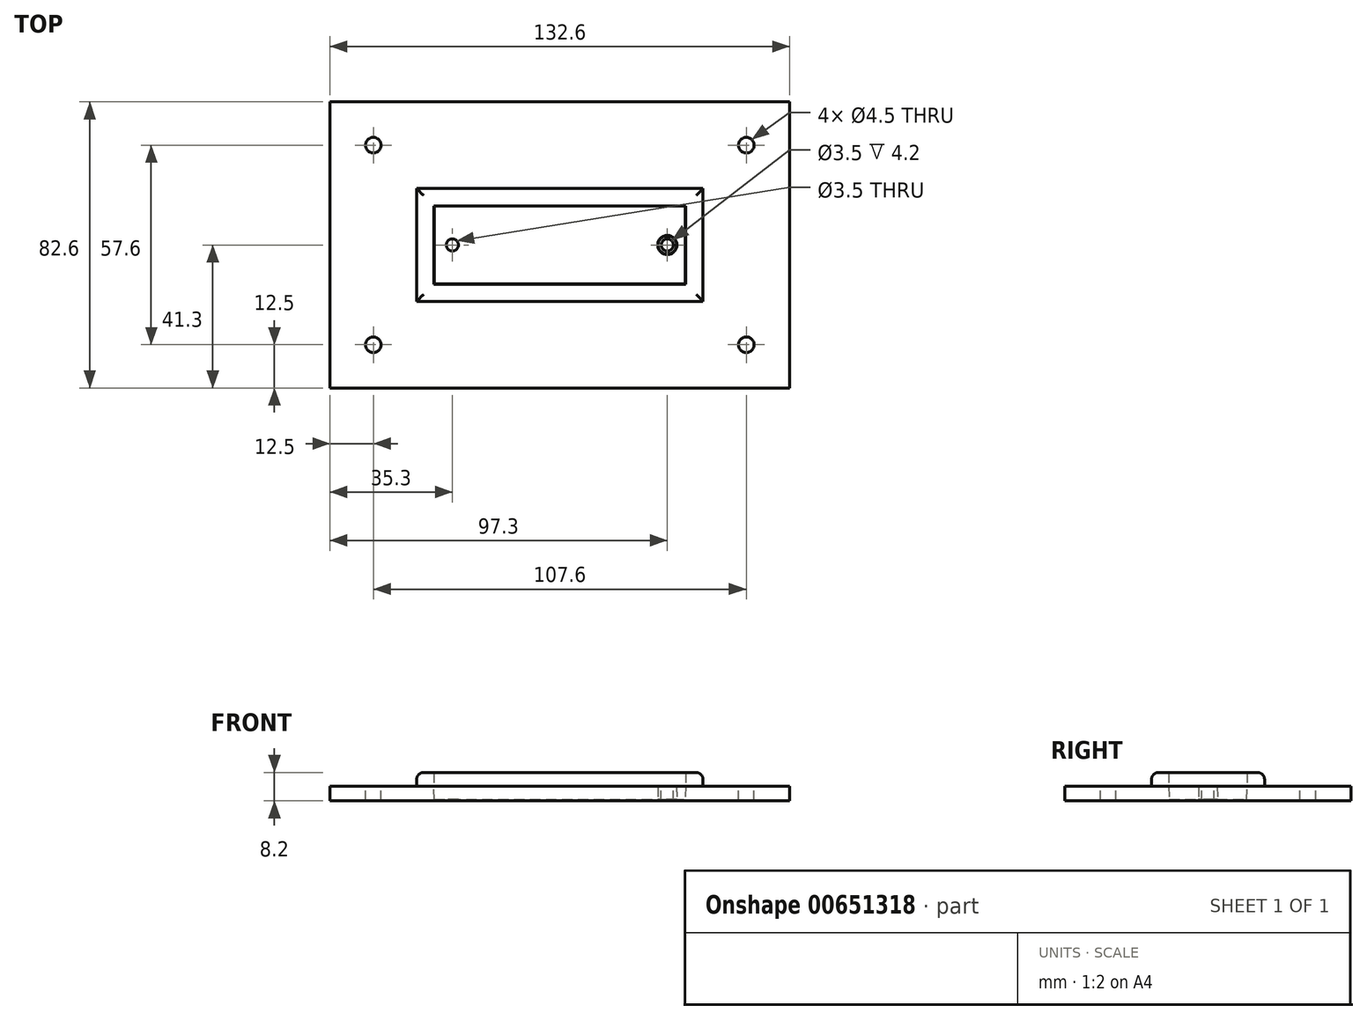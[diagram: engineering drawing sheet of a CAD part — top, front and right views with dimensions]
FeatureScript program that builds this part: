
annotation { "Feature Type Name" : "Feature", "Feature Type Description" : "" }
export const myFeature = defineFeature(function(context is Context, id is Id, definition is map)
    precondition{}
    {
        {
            var Q0;
            Q0=qCreatedBy(makeId("Top.planeOp"),FACE);
            var sketch = newSketch(context, id + "F0", { "sketchPlane" : qUnion([Q0])});
            skLineSegment(sketch, "E0.bottom", {"start": v(36, -11) * mm, "end": v(-36, -11) * mm});
            skLineSegment(sketch, "E0.top", {"start": v(36, 11) * mm, "end": v(-36, 11) * mm});
            skLineSegment(sketch, "E0.left", {"start": v(36, -11) * mm, "end": v(36, 11) * mm});
            skLineSegment(sketch, "E0.right", {"start": v(-36, -11) * mm, "end": v(-36, 11) * mm});
            skPoint(sketch, "E0.middle", {"position": v(0, 0) * mm});
            skCircle(sketch, "E1", {"center": v(-31, 0) * mm, "radius": 2 * mm});
            skLineSegment(sketch, "E2", {"start": v(0, 30.73) * mm, "end": v(0, -25.9) * mm, "construction": true});
            skCircle(sketch, "E3.MirrorC", {"center": v(31, 0) * mm, "radius": 2 * mm});
            skLineSegment(sketch, "E4.0", {"start": v(36.3, 11.3) * mm, "end": v(-36.3, 11.3) * mm});
            skLineSegment(sketch, "E4.1", {"start": v(36.3, -11.3) * mm, "end": v(36.3, 11.3) * mm});
            skLineSegment(sketch, "E4.2", {"start": v(36.3, -11.3) * mm, "end": v(-36.3, -11.3) * mm});
            skLineSegment(sketch, "E4.3", {"start": v(-36.3, -11.3) * mm, "end": v(-36.3, 11.3) * mm});
            skLineSegment(sketch, "E5.0", {"start": v(41.3, 16.3) * mm, "end": v(-41.3, 16.3) * mm});
            skLineSegment(sketch, "E5.1", {"start": v(41.3, -16.3) * mm, "end": v(41.3, 16.3) * mm});
            skLineSegment(sketch, "E5.2", {"start": v(41.3, -16.3) * mm, "end": v(-41.3, -16.3) * mm});
            skLineSegment(sketch, "E5.3", {"start": v(-41.3, -16.3) * mm, "end": v(-41.3, 16.3) * mm});
            skLineSegment(sketch, "E6", {"start": v(-77.14, 0) * mm, "end": v(78.88, 0) * mm, "construction": true});
            skSolve(sketch);
        }
        {
            var Q0;
            Q0=qCreatedBy(makeId("Top.planeOp"),FACE);
            var sketch = newSketch(context, id + "F1", { "sketchPlane" : qUnion([Q0])});
            skLineSegment(sketch, "E7.bottom", {"start": v(66.3, -41.3) * mm, "end": v(-66.3, -41.3) * mm});
            skLineSegment(sketch, "E7.top", {"start": v(66.3, 41.3) * mm, "end": v(-66.3, 41.3) * mm});
            skLineSegment(sketch, "E7.left", {"start": v(66.3, -41.3) * mm, "end": v(66.3, 41.3) * mm});
            skLineSegment(sketch, "E7.right", {"start": v(-66.3, -41.3) * mm, "end": v(-66.3, 41.3) * mm});
            skPoint(sketch, "E7.middle", {"position": v(0, 0) * mm});
            skCircle(sketch, "E8", {"center": v(-53.8, 28.8) * mm, "radius": 2.25 * mm});
            skCircle(sketch, "E9.MirrorC", {"center": v(-53.8, -28.8) * mm, "radius": 2.25 * mm});
            skCircle(sketch, "E10.MirrorC", {"center": v(53.8, 28.8) * mm, "radius": 2.25 * mm});
            skCircle(sketch, "E11.MirrorC", {"center": v(53.8, -28.8) * mm, "radius": 2.25 * mm});
            skSolve(sketch);
        }
        {
            var Q0;
            Q0=makeQuery(id+"F1.imprint","IMPRINT",FACE,{"disambiguationData":[TD([[makeQuery(id+"F1.imprint","IMPRINT",EDGE,{"derivedFrom":sQuery(id+"F1.wireOp",EDGE,"E7.bottom")}),-1.0]])]});
            extrude(context, id + "F2", {"entities" : qUnion([Q0]), "oppositeDirection" : true, "depth" : 4.2 * mm, "offsetDistance" : 25 * mm});
        }
        {
            var Q0;
            Q0=makeQuery(id+"F0.imprint","IMPRINT",FACE,{"disambiguationData":[TD([[makeQuery(id+"F0.imprint","IMPRINT",EDGE,{"derivedFrom":sQuery(id+"F0.wireOp",EDGE,"E4.0")}),-1.0]])]});
            extrude(context, id + "F3", {"entities" : qUnion([Q0]), "operationType" : NewBodyOperationType.ADD, "depth" : 4 * mm, "offsetDistance" : 25 * mm});
        }
        {
            var Q0;
            Q0=makeQuery(id+"F3.boolean.opBoolean","SPLIT",FACE,{"disambiguationData":[TD([makeQuery(id+"F3.opExtrude","SWEPT_FACE",FACE,{"disambiguationData":[OSD([sQuery(id+"F0.wireOp",EDGE,"E4.0")])]})])],"derivedFrom":makeQuery(id+"F2.opExtrude","CAP_FACE",FACE,{"disambiguationData":[OSD([sQuery(id+"F1.wireOp",EDGE,"E7.bottom"),sQuery(id+"F1.wireOp",EDGE,"E7.top"),sQuery(id+"F1.wireOp",EDGE,"E7.left"),sQuery(id+"F1.wireOp",EDGE,"E7.right"),sQuery(id+"F1.wireOp",EDGE,"E8"),sQuery(id+"F1.wireOp",EDGE,"E9.MirrorC"),sQuery(id+"F1.wireOp",EDGE,"E10.MirrorC"),sQuery(id+"F1.wireOp",EDGE,"E11.MirrorC")])],"isStart":true})});
            var sketch = newSketch(context, id + "F4", { "sketchPlane" : qUnion([Q0])});
            skPoint(sketch, "E12", {"position": v(-31, 0) * mm});
            skPoint(sketch, "E13", {"position": v(31, 0) * mm});
            skCircle(sketch, "E14", {"center": v(-31, 0) * mm, "radius": 2.65 * mm});
            skCircle(sketch, "E15.MirrorC", {"center": v(31, 0) * mm, "radius": 2.65 * mm});
            skSolve(sketch);
        }
        {
            var Q0;
            Q0=makeQuery(id+"F4.imprint","IMPRINT",FACE,{"disambiguationData":[TD([[makeQuery(id+"F4.imprint","IMPRINT",EDGE,{"derivedFrom":sQuery(id+"F4.wireOp",EDGE,"E14")}),1.0]])]});
            var Q1;
            Q1=makeQuery(id+"F4.imprint","IMPRINT",FACE,{"disambiguationData":[TD([[makeQuery(id+"F4.imprint","IMPRINT",EDGE,{"derivedFrom":sQuery(id+"F4.wireOp",EDGE,"E15.MirrorC")}),-1.0]])]});
            extrude(context, id + "F5", {"entities" : qUnion([Q0, Q1]), "operationType" : NewBodyOperationType.REMOVE, "oppositeDirection" : true, "depth" : 3.8 * mm, "offsetDistance" : 25 * mm, "hasDraft" : true, "draftAngle" : 1.6 * degree, "draftPullDirection" : true});
        }
        {
            var Q0;
            Q0=makeQuery(id+"F4.imprint","IMPRINT",FACE,{"disambiguationData":[TD([[makeQuery(id+"F4.imprint","IMPRINT",EDGE,{"derivedFrom":sQuery(id+"F4.wireOp",EDGE,"E14")}),-1.0]])]});
            var sketch = newSketch(context, id + "F6", { "sketchPlane" : qUnion([Q0])});
            skPoint(sketch, "E16.0", {"position": v(31, 0) * mm});
            skPoint(sketch, "E17.0", {"position": v(-31, 0) * mm});
            skCircle(sketch, "E18", {"center": v(31, 0) * mm, "radius": 1.75 * mm});
            skCircle(sketch, "E19", {"center": v(-31, 0) * mm, "radius": 1.75 * mm});
            skSolve(sketch);
        }
        {
            var Q0;
            Q0 = qSketchRegion(id + "F6", true);
            extrude(context, id + "F7", {"entities" : qUnion([Q0]), "operationType" : NewBodyOperationType.REMOVE, "endBound" : BoundingType.THROUGH_ALL, "oppositeDirection" : true, "depth" : 25 * mm, "offsetDistance" : 25 * mm});
        }
        {
            var Q0;
            Q0=makeQuery(id+"F3.opExtrude","CAP_EDGE",EDGE,{"disambiguationData":[OSD([sQuery(id+"F0.wireOp",EDGE,"E5.0")])],"isStart":true});
            var Q1;
            Q1=makeQuery(id+"F3.opExtrude","CAP_EDGE",EDGE,{"disambiguationData":[OSD([sQuery(id+"F0.wireOp",EDGE,"E5.3")])],"isStart":true});
            var Q2;
            Q2=makeQuery(id+"F3.opExtrude","CAP_EDGE",EDGE,{"disambiguationData":[OSD([sQuery(id+"F0.wireOp",EDGE,"E5.2")])],"isStart":true});
            var Q3;
            Q3=makeQuery(id+"F3.opExtrude","CAP_EDGE",EDGE,{"disambiguationData":[OSD([sQuery(id+"F0.wireOp",EDGE,"E5.1")])],"isStart":true});
            var Q4;
            Q4=makeQuery(id+"F3.opExtrude","CAP_EDGE",EDGE,{"disambiguationData":[OSD([sQuery(id+"F0.wireOp",EDGE,"E5.2")])],"isStart":false});
            var Q5;
            Q5=makeQuery(id+"F3.opExtrude","CAP_EDGE",EDGE,{"disambiguationData":[OSD([sQuery(id+"F0.wireOp",EDGE,"E5.1")])],"isStart":false});
            var Q6;
            Q6=makeQuery(id+"F3.opExtrude","CAP_EDGE",EDGE,{"disambiguationData":[OSD([sQuery(id+"F0.wireOp",EDGE,"E5.0")])],"isStart":false});
            var Q7;
            Q7=makeQuery(id+"F3.opExtrude","CAP_EDGE",EDGE,{"disambiguationData":[OSD([sQuery(id+"F0.wireOp",EDGE,"E5.3")])],"isStart":false});
            fillet(context, id + "F8", {"entities" : qUnion([Q0, Q1, Q2, Q3, Q4, Q5, Q6, Q7]), "radius" : 2 * mm, "tangentPropagation" : true, "allowEdgeOverflow" : false});
        }
    });
